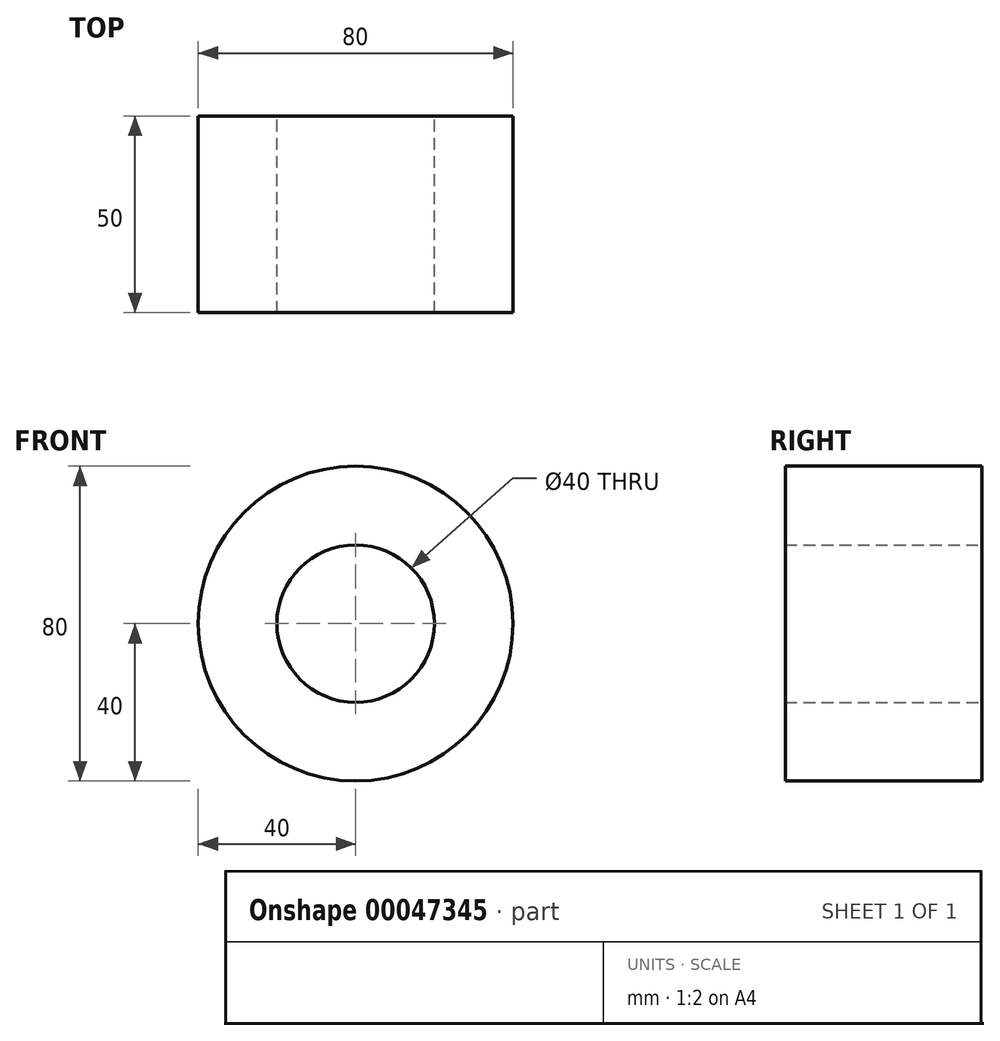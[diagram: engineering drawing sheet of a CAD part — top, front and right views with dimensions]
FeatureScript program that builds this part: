
annotation { "Feature Type Name" : "Feature", "Feature Type Description" : "" }
export const myFeature = defineFeature(function(context is Context, id is Id, definition is map)
    precondition{}
    {
        {
            var Q0;
            Q0=qCreatedBy(makeId("Front.planeOp"),FACE);
            var sketch = newSketch(context, id + "F0", { "sketchPlane" : qUnion([Q0])});
            skCircle(sketch, "E0", {"center": v(0, 0) * mm, "radius": 40 * mm});
            skCircle(sketch, "E1", {"center": v(0, 0) * mm, "radius": 20 * mm});
            skSolve(sketch);
        }
        {
            var Q0;
            Q0 = qSketchRegion(id + "F0", true);
            extrude(context, id + "F1", {"entities" : qUnion([Q0]), "depth" : 50 * mm});
        }
    });
